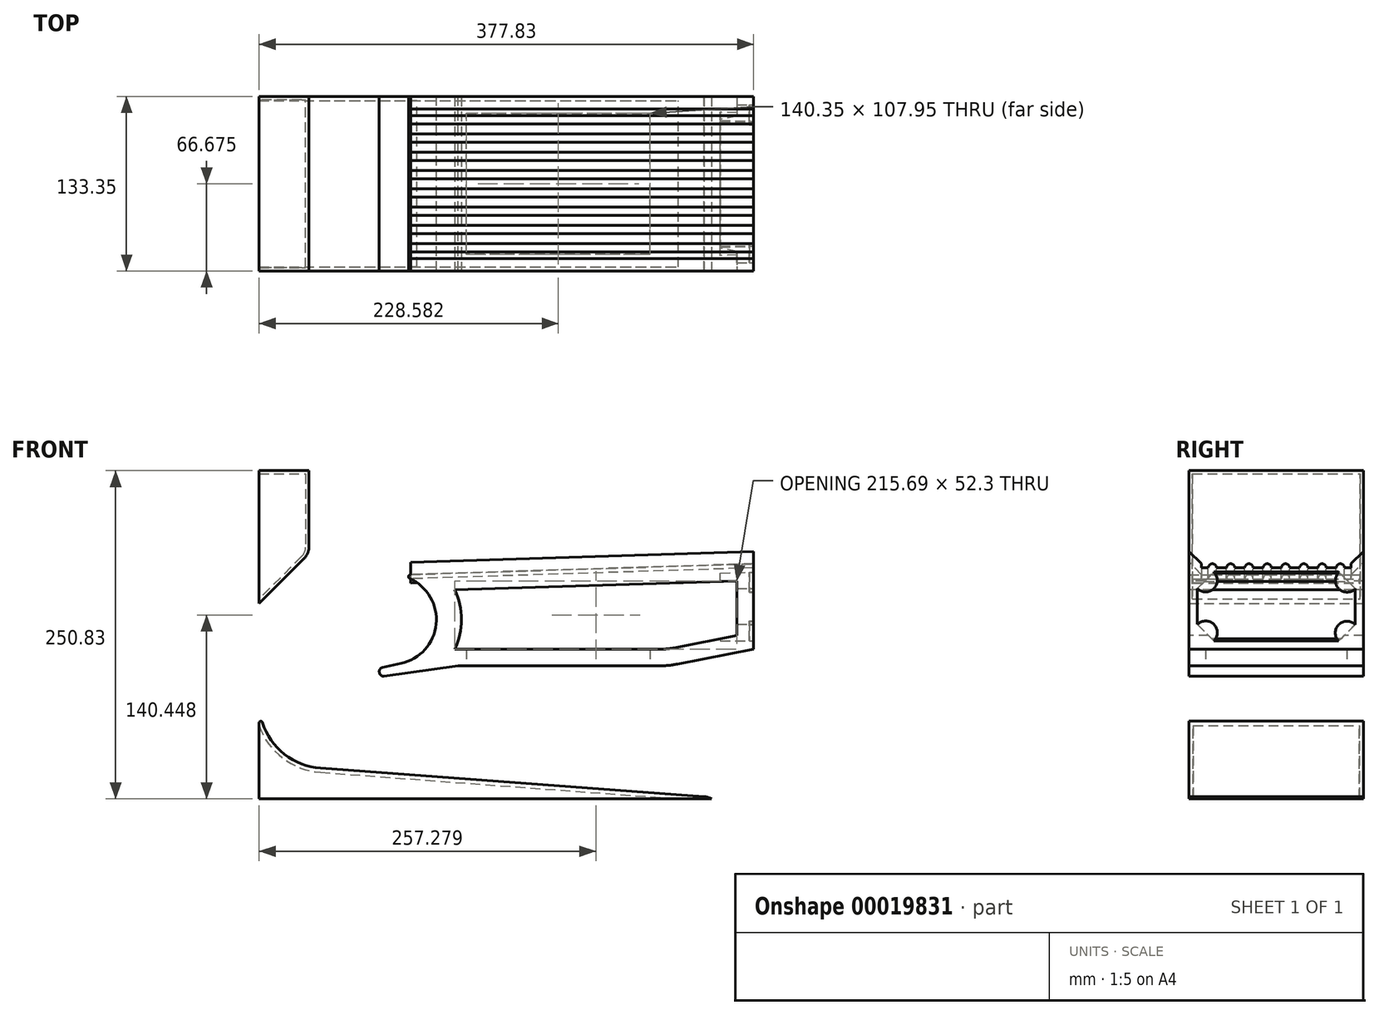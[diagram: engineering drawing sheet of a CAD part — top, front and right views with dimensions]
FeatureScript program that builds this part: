
annotation { "Feature Type Name" : "Feature", "Feature Type Description" : "" }
export const myFeature = defineFeature(function(context is Context, id is Id, definition is map)
    precondition{}
    {
        {
            var Q0;
            Q0=qCreatedBy(makeId("Front.planeOp"),FACE);
            var sketch = newSketch(context, id + "F0", { "sketchPlane" : qUnion([Q0])});
            skLineSegment(sketch, "E0.bottom", {"start": v(0, 0) * mm, "end": v(377.82, 0) * mm});
            skLineSegment(sketch, "E0.top", {"start": v(0, 250.83) * mm, "end": v(377.83, 250.83) * mm});
            skLineSegment(sketch, "E0.left", {"start": v(0, 74.15) * mm, "end": v(0, 250.82) * mm});
            skLineSegment(sketch, "E0.right", {"start": v(377.83, 0) * mm, "end": v(377.83, 250.83) * mm});
            skCircle(sketch, "E1", {"center": v(75.12, 58.13) * mm, "radius": 33.02 * mm});
            skArc(sketch, "E2", {"start": v(340.31, 1.68) * mm, "mid": v(359.23, 5.64) * mm, "end": v(373.15, 19.05) * mm});
            skLineSegment(sketch, "E3", {"start": v(377.83, 19.05) * mm, "end": v(373.15, 19.05) * mm});
            skLineSegment(sketch, "E4", {"start": v(47.03, 23.5) * mm, "end": v(340.31, 1.68) * mm});
            skPoint(sketch, "E5.visualSharp", {"position": v(0, 26.99) * mm});
            skArc(sketch, "E5.filletArc", {"start": v(2.48, 58.48) * mm, "mid": v(19.43, 34.2) * mm, "end": v(47.03, 23.5) * mm});
            skCircle(sketch, "E6.1.0.0", {"center": v(141.46, 52.73) * mm, "radius": 33.02 * mm});
            skCircle(sketch, "E6.2.0.0", {"center": v(207.8, 47.34) * mm, "radius": 33.02 * mm});
            skCircle(sketch, "E6.3.0.0", {"center": v(274.13, 41.94) * mm, "radius": 33.02 * mm});
            skCircle(sketch, "E6.4.0.0", {"center": v(340.47, 36.54) * mm, "radius": 33.02 * mm});
            skLineSegment(sketch, "E6.direction1", {"start": v(75.12, 58.13) * mm, "end": v(141.46, 52.73) * mm, "construction": true});
            skCircle(sketch, "E7", {"center": v(34.64, 111.21) * mm, "radius": 33.02 * mm});
            skLineSegment(sketch, "E8", {"start": v(377.83, 179.7) * mm, "end": v(115.72, 171.4) * mm});
            skArc(sketch, "E9.trimOffspring", {"start": v(108.42, 103.52) * mm, "mid": v(135.29, 133.5) * mm, "end": v(115.13, 168.36) * mm});
            skPoint(sketch, "E10.visualSharp", {"position": v(94.86, 170.74) * mm});
            skArc(sketch, "E10.filletArc", {"start": v(115.72, 171.4) * mm, "mid": v(114.21, 170.12) * mm, "end": v(115.13, 168.36) * mm});
            skCircle(sketch, "E11", {"center": v(96.26, 138.02) * mm, "radius": 33.02 * mm});
            skLineSegment(sketch, "E12", {"start": v(94.32, 100.47) * mm, "end": v(108.42, 103.52) * mm});
            skLineSegment(sketch, "E13", {"start": v(91.89, 96.7) * mm, "end": v(91.98, 96.26) * mm});
            skLineSegment(sketch, "E14", {"start": v(95.52, 93.78) * mm, "end": v(152.06, 101.6) * mm});
            skPoint(sketch, "E15.visualSharp", {"position": v(91.22, 99.8) * mm});
            skArc(sketch, "E15.filletArc", {"start": v(94.32, 100.47) * mm, "mid": v(92.32, 99.09) * mm, "end": v(91.89, 96.7) * mm});
            skPoint(sketch, "E16.visualSharp", {"position": v(92.6, 93.38) * mm});
            skArc(sketch, "E16.filletArc", {"start": v(91.98, 96.26) * mm, "mid": v(93.26, 94.32) * mm, "end": v(95.52, 93.78) * mm});
            skCircle(sketch, "E17.1.0.0", {"center": v(139.77, 207.48) * mm, "radius": 33.02 * mm});
            skCircle(sketch, "E17.2.0.0", {"center": v(206.9, 209.08) * mm, "radius": 33.02 * mm});
            skCircle(sketch, "E17.3.0.0", {"center": v(274.03, 210.68) * mm, "radius": 33.02 * mm});
            skCircle(sketch, "E17.4.0.0", {"center": v(341.17, 212.28) * mm, "radius": 33.02 * mm});
            skLineSegment(sketch, "E17.direction1", {"start": v(72.64, 205.88) * mm, "end": v(139.77, 207.48) * mm, "construction": true});
            skCircle(sketch, "E18.1.0.0", {"center": v(72.02, 201.09) * mm, "radius": 33.02 * mm});
            skLineSegment(sketch, "E19", {"start": v(38.1, 250.83) * mm, "end": v(38.1, 192.59) * mm});
            skLineSegment(sketch, "E20", {"start": v(34.38, 183.6) * mm, "end": v(0, 149.22) * mm});
            skPoint(sketch, "E21.visualSharp", {"position": v(38.1, 187.32) * mm});
            skArc(sketch, "E21.filletArc", {"start": v(34.38, 183.6) * mm, "mid": v(37.13, 187.73) * mm, "end": v(38.1, 192.59) * mm});
            skLineSegment(sketch, "E22", {"start": v(0, 0) * mm, "end": v(0, 58.09) * mm});
            skCircle(sketch, "E23", {"center": v(374.8, 54.39) * mm, "radius": 33.02 * mm});
            skLineSegment(sketch, "E24", {"start": v(305.1, 101.6) * mm, "end": v(152.06, 101.6) * mm});
            skPoint(sketch, "E25.orphan", {"position": v(312.44, 101.6) * mm});
            skLineSegment(sketch, "E26", {"start": v(319.64, 103) * mm, "end": v(377.83, 114.3) * mm});
            skPoint(sketch, "E27.orphan", {"position": v(377.83, 101.6) * mm});
            skArc(sketch, "E28.filletArc", {"start": v(305.1, 101.6) * mm, "mid": v(312.4, 101.95) * mm, "end": v(319.64, 103) * mm});
            skPoint(sketch, "E29.visualSharp", {"position": v(0, 74.15) * mm});
            skArc(sketch, "E29.filletArc", {"start": v(2.48, 58.48) * mm, "mid": v(1.07, 59.34) * mm, "end": v(0, 58.09) * mm});
            skSolve(sketch);
        }
        {
            var Q0;
            {var subQ2=sQuery(id+"F0.wireOp",EDGE,"E0.bottom");Q0=makeQuery(id+"F0.imprint","IMPRINT",FACE,{"disambiguationData":[TD([[makeQuery(id+"F0.imprint","IMPRINT",EDGE,{"derivedFrom":subQ2}),1.0]])]});}
            var Q1;
            {var subQ1=sQuery(id+"F0.wireOp",EDGE,"E8");Q1=makeQuery(id+"F0.imprint","IMPRINT",FACE,{"disambiguationData":[TD([[makeQuery(id+"F0.imprint","IMPRINT",EDGE,{"derivedFrom":subQ1}),1.0]])]});}
            var Q2;
            {var subQ1=sQuery(id+"F0.wireOp",EDGE,"E19");Q2=makeQuery(id+"F0.imprint","IMPRINT",FACE,{"disambiguationData":[TD([[makeQuery(id+"F0.imprint","IMPRINT",EDGE,{"derivedFrom":subQ1}),-1.0]])]});}
            extrude(context, id + "F1", {"entities" : qUnion([Q0, Q1, Q2]), "depth" : 133.35 * mm});
        }
        {
            var Q0;
            {var subQ0=sQuery(id+"F0.wireOp",EDGE,"E0.right");Q0=makeQuery(id+"F1.opExtrude","SWEPT_FACE",FACE,{"disambiguationData":[OSD([subQ0]),TDD([makeQuery(id+"F0.imprint","IMPRINT",EDGE,{"disambiguationData":[TD([[makeQuery(id+"F0.imprint","INTERSECT",VERTEX,{"derivedFrom":[subQ0,sQuery(id+"F0.wireOp",EDGE,"E8")]}),1.0]])],"derivedFrom":subQ0})])]});}
            var sketch = newSketch(context, id + "F2", { "sketchPlane" : qUnion([Q0])});
            skLineSegment(sketch, "E30.bottom", {"start": v(0, 179.7) * mm, "end": v(-98.4, 179.7) * mm});
            skLineSegment(sketch, "E30.top", {"start": v(0, 188.78) * mm, "end": v(-98.4, 188.78) * mm});
            skLineSegment(sketch, "E30.left", {"start": v(0, 179.7) * mm, "end": v(0, 188.78) * mm});
            skLineSegment(sketch, "E30.right", {"start": v(-98.4, 179.7) * mm, "end": v(-98.4, 188.78) * mm});
            skSolve(sketch);
        }
        {
            var Q0;
            Q0=makeQuery(id+"F1.opExtrude","CAP_FACE",FACE,{"disambiguationData":[OSD([sQuery(id+"F0.wireOp",EDGE,"E0.right"),sQuery(id+"F0.wireOp",EDGE,"E8"),sQuery(id+"F0.wireOp",EDGE,"E9.trimOffspring"),sQuery(id+"F0.wireOp",EDGE,"E10.filletArc"),sQuery(id+"F0.wireOp",EDGE,"E12"),sQuery(id+"F0.wireOp",EDGE,"E13"),sQuery(id+"F0.wireOp",EDGE,"E14"),sQuery(id+"F0.wireOp",EDGE,"E15.filletArc"),sQuery(id+"F0.wireOp",EDGE,"E16.filletArc"),sQuery(id+"F0.wireOp",EDGE,"E24"),sQuery(id+"F0.wireOp",EDGE,"E26"),sQuery(id+"F0.wireOp",EDGE,"E28.filletArc")])],"isStart":false});
            var sketch = newSketch(context, id + "F3", { "sketchPlane" : qUnion([Q0])});
            skLineSegment(sketch, "E31.0", {"start": v(365.13, 166.6) * mm, "end": v(149.44, 159.76) * mm});
            skLineSegment(sketch, "E32.0", {"start": v(305.1, 114.3) * mm, "end": v(149.43, 114.3) * mm});
            skArc(sketch, "E32.1", {"start": v(305.1, 114.3) * mm, "mid": v(311.19, 114.6) * mm, "end": v(317.21, 115.46) * mm});
            skLineSegment(sketch, "E32.2", {"start": v(317.21, 115.46) * mm, "end": v(365.13, 124.77) * mm});
            skLineSegment(sketch, "E32.3", {"start": v(365.13, 124.77) * mm, "end": v(365.13, 166.6) * mm});
            skArc(sketch, "E33.0", {"start": v(149.43, 114.3) * mm, "mid": v(154.52, 137.03) * mm, "end": v(149.44, 159.76) * mm});
            skSolve(sketch);
        }
        {
            var Q0;
            {var subQ6=sQuery(id+"F2.wireOp",EDGE,"E30.bottom");Q0=makeQuery(id+"F2.imprint","IMPRINT",FACE,{"disambiguationData":[TD([[makeQuery(id+"F2.imprint","IMPRINT",EDGE,{"derivedFrom":subQ6}),-1.0]])]});}
            var sketch = newSketch(context, id + "F4", { "sketchPlane" : qUnion([Q0])});
            skLineSegment(sketch, "E34.bottom", {"start": v(-114.3, 173.36) * mm, "end": v(-19.05, 173.36) * mm});
            skLineSegment(sketch, "E34.top", {"start": v(-114.3, 120.65) * mm, "end": v(-19.05, 120.65) * mm});
            skLineSegment(sketch, "E34.left", {"start": v(-127, 160.66) * mm, "end": v(-127, 133.35) * mm});
            skLineSegment(sketch, "E34.right", {"start": v(-6.35, 160.66) * mm, "end": v(-6.35, 133.35) * mm});
            skLineSegment(sketch, "E35", {"start": v(-127, 160.66) * mm, "end": v(-114.3, 173.36) * mm});
            skPoint(sketch, "E36.orphan", {"position": v(-127, 173.36) * mm});
            skLineSegment(sketch, "E37.MirrorCS", {"start": v(-6.35, 160.66) * mm, "end": v(-19.05, 173.36) * mm});
            skLineSegment(sketch, "E38.MirrorCS", {"start": v(-6.35, 133.35) * mm, "end": v(-19.05, 120.65) * mm});
            skPoint(sketch, "E39.start.orphan", {"position": v(-6.35, 147) * mm});
            skPoint(sketch, "E40.start.orphan", {"position": v(-66.68, 120.65) * mm});
            skPoint(sketch, "E41.orphan", {"position": v(-127, 120.65) * mm});
            skPoint(sketch, "E42.orphan", {"position": v(-6.35, 120.65) * mm});
            skPoint(sketch, "E43.orphan", {"position": v(-6.35, 173.36) * mm});
            skLineSegment(sketch, "E44.MirrorCS", {"start": v(-127, 133.35) * mm, "end": v(-114.3, 120.65) * mm});
            skPoint(sketch, "E45.end.orphan", {"position": v(-127, 147) * mm});
            skSolve(sketch);
        }
        {
            var Q0;
            Q0=makeQuery(id+"F1.opExtrude","CAP_FACE",FACE,{"disambiguationData":[OSD([sQuery(id+"F0.wireOp",EDGE,"E0.bottom"),sQuery(id+"F0.wireOp",EDGE,"E0.right"),sQuery(id+"F0.wireOp",EDGE,"E2"),sQuery(id+"F0.wireOp",EDGE,"E3"),sQuery(id+"F0.wireOp",EDGE,"E4"),sQuery(id+"F0.wireOp",EDGE,"E5.filletArc"),sQuery(id+"F0.wireOp",EDGE,"E22")])],"isStart":false});
            var sketch = newSketch(context, id + "F5", { "sketchPlane" : qUnion([Q0])});
            skLineSegment(sketch, "E46.bottom", {"start": v(377.83, 0) * mm, "end": v(345.84, 0) * mm});
            skLineSegment(sketch, "E46.top", {"start": v(377.83, 22.34) * mm, "end": v(345.84, 22.34) * mm});
            skLineSegment(sketch, "E46.left", {"start": v(377.83, 0) * mm, "end": v(377.83, 22.34) * mm});
            skLineSegment(sketch, "E46.right", {"start": v(345.84, 4.83) * mm, "end": v(345.84, 22.34) * mm});
            skLineSegment(sketch, "E47", {"start": v(345.84, 0) * mm, "end": v(345.64, 0.1) * mm});
            skLineSegment(sketch, "E48", {"start": v(340.31, 1.68) * mm, "end": v(339.94, 1.7) * mm});
            skPoint(sketch, "E49.visualSharp", {"position": v(342.98, 1.59) * mm});
            skArc(sketch, "E49.filletArc", {"start": v(345.64, 0.1) * mm, "mid": v(342.88, 1.24) * mm, "end": v(339.94, 1.7) * mm});
            skLineSegment(sketch, "E50", {"start": v(339.94, 1.7) * mm, "end": v(345.84, 4.83) * mm});
            skSolve(sketch);
        }
        {
            var Q0;
            Q0 = qSketchRegion(id + "F5", true);
            extrude(context, id + "F6", {"entities" : qUnion([Q0]), "operationType" : NewBodyOperationType.REMOVE, "endBound" : BoundingType.THROUGH_ALL, "oppositeDirection" : true, "depth" : 25.4 * mm});
        }
        {
            var Q0;
            Q0=makeQuery(id+"F1.opExtrude","SWEPT_FACE",FACE,{"disambiguationData":[OSD([sQuery(id+"F0.wireOp",EDGE,"E0.left")])]});
            shell(context, id + "F7", {"entities" : qUnion([Q0]), "thickness" : 2.54 * mm});
        }
        {
            var Q0;
            {var subQ6=sQuery(id+"F2.wireOp",EDGE,"E30.bottom");Q0=makeQuery(id+"F2.imprint","IMPRINT",FACE,{"disambiguationData":[TD([[makeQuery(id+"F2.imprint","IMPRINT",EDGE,{"derivedFrom":subQ6}),-1.0]])]});}
            var sketch = newSketch(context, id + "F8", { "sketchPlane" : qUnion([Q0])});
            skLineSegment(sketch, "E51", {"start": v(-123.83, 176.53) * mm, "end": v(-118.74, 176.53) * mm});
            skArc(sketch, "E52", {"start": v(-112.4, 176.53) * mm, "mid": v(-115.57, 179.7) * mm, "end": v(-118.75, 176.53) * mm});
            skArc(sketch, "E53.1.0.0", {"start": v(-98.43, 176.53) * mm, "mid": v(-101.6, 179.7) * mm, "end": v(-104.78, 176.53) * mm});
            skArc(sketch, "E53.2.0.0", {"start": v(-84.46, 176.53) * mm, "mid": v(-87.63, 179.7) * mm, "end": v(-90.8, 176.53) * mm});
            skArc(sketch, "E53.3.0.0", {"start": v(-70.49, 176.53) * mm, "mid": v(-73.66, 179.7) * mm, "end": v(-76.84, 176.53) * mm});
            skArc(sketch, "E53.4.0.0", {"start": v(-56.52, 176.53) * mm, "mid": v(-59.7, 179.7) * mm, "end": v(-62.87, 176.53) * mm});
            skArc(sketch, "E53.5.0.0", {"start": v(-42.55, 176.53) * mm, "mid": v(-45.72, 179.7) * mm, "end": v(-48.9, 176.53) * mm});
            skArc(sketch, "E53.6.0.0", {"start": v(-28.58, 176.53) * mm, "mid": v(-31.75, 179.7) * mm, "end": v(-34.93, 176.53) * mm});
            skArc(sketch, "E53.7.0.0", {"start": v(-14.6, 176.53) * mm, "mid": v(-17.78, 179.7) * mm, "end": v(-20.96, 176.53) * mm});
            skLineSegment(sketch, "E53.direction1", {"start": v(-112.4, 176.53) * mm, "end": v(-101.6, 176.53) * mm, "construction": true});
            skLineSegment(sketch, "E54.trimOffspring", {"start": v(-112.4, 176.53) * mm, "end": v(-104.78, 176.53) * mm});
            skLineSegment(sketch, "E55.trimOffspring", {"start": v(-70.49, 176.53) * mm, "end": v(-62.87, 176.53) * mm});
            skLineSegment(sketch, "E56.trimOffspring", {"start": v(-28.58, 176.53) * mm, "end": v(-20.96, 176.53) * mm});
            skLineSegment(sketch, "E57.trimOffspring", {"start": v(-14.6, 176.53) * mm, "end": v(-9.53, 176.53) * mm});
            skLineSegment(sketch, "E58", {"start": v(-42.55, 176.53) * mm, "end": v(-34.93, 176.53) * mm});
            skLineSegment(sketch, "E59", {"start": v(-56.52, 176.53) * mm, "end": v(-48.9, 176.53) * mm});
            skLineSegment(sketch, "E60", {"start": v(-84.46, 176.53) * mm, "end": v(-76.84, 176.53) * mm});
            skLineSegment(sketch, "E61", {"start": v(-98.43, 176.53) * mm, "end": v(-90.8, 176.53) * mm});
            skLineSegment(sketch, "E62", {"start": v(-123.83, 176.53) * mm, "end": v(-123.83, 179.7) * mm});
            skLineSegment(sketch, "E63", {"start": v(-115.57, 179.7) * mm, "end": v(-123.83, 179.7) * mm});
            skLineSegment(sketch, "E64", {"start": v(-115.57, 179.7) * mm, "end": v(-9.52, 179.7) * mm});
            skLineSegment(sketch, "E65", {"start": v(-9.53, 176.53) * mm, "end": v(-9.53, 179.7) * mm});
            skPoint(sketch, "E66.orphan", {"position": v(0, 176.53) * mm});
            skPoint(sketch, "E67.orphan", {"position": v(0, 179.7) * mm});
            skPoint(sketch, "E68.start.orphan", {"position": v(-133.35, 176.53) * mm});
            skSolve(sketch);
        }
        {
            var Q0;
            Q0 = qSketchRegion(id + "F8", true);
            var Q1;
            Q1=makeQuery(id+"F1.opExtrude","CAP_EDGE",EDGE,{"disambiguationData":[OSD([sQuery(id+"F0.wireOp",EDGE,"E8")])],"isStart":false});
            sweep(context, id + "F9", {"operationType" : NewBodyOperationType.REMOVE, "profiles" : qUnion([Q0]), "path" : qUnion([Q1])});
        }
        {
            var Q0;
            {var subQ6=sQuery(id+"F2.wireOp",EDGE,"E30.bottom");Q0=makeQuery(id+"F2.imprint","IMPRINT",FACE,{"disambiguationData":[TD([[makeQuery(id+"F2.imprint","IMPRINT",EDGE,{"derivedFrom":subQ6}),-1.0]])]});}
            var sketch = newSketch(context, id + "F10", { "sketchPlane" : qUnion([Q0])});
            skLineSegment(sketch, "E69", {"start": v(-133.35, 189.1) * mm, "end": v(-133.35, 179.58) * mm});
            skLineSegment(sketch, "E70", {"start": v(-133.35, 179.58) * mm, "end": v(-123.83, 179.58) * mm});
            skLineSegment(sketch, "E71", {"start": v(-123.83, 179.58) * mm, "end": v(-123.83, 179.7) * mm});
            skLineSegment(sketch, "E72", {"start": v(-123.83, 179.7) * mm, "end": v(-133.35, 189.1) * mm});
            skLineSegment(sketch, "E73.MirrorCS", {"start": v(-9.52, 179.7) * mm, "end": v(0, 189.1) * mm});
            skLineSegment(sketch, "E74.MirrorCS", {"start": v(-9.52, 179.58) * mm, "end": v(-9.52, 179.7) * mm});
            skLineSegment(sketch, "E75.MirrorCS", {"start": v(0, 179.58) * mm, "end": v(-9.53, 179.58) * mm});
            skLineSegment(sketch, "E76.MirrorCS", {"start": v(0, 189.1) * mm, "end": v(0, 179.58) * mm});
            skSolve(sketch);
        }
        {
            var Q0;
            Q0 = qSketchRegion(id + "F10", true);
            var Q1;
            Q1=makeQuery(id+"F1.opExtrude","CAP_EDGE",EDGE,{"disambiguationData":[OSD([sQuery(id+"F0.wireOp",EDGE,"E8")])],"isStart":false});
            sweep(context, id + "F11", {"operationType" : NewBodyOperationType.ADD, "profiles" : qUnion([Q0]), "path" : qUnion([Q1])});
        }
        {
            var Q0;
            Q0 = qSketchRegion(id + "F3", true);
            extrude(context, id + "F12", {"entities" : qUnion([Q0]), "operationType" : NewBodyOperationType.REMOVE, "endBound" : BoundingType.THROUGH_ALL, "oppositeDirection" : true, "depth" : 25.4 * mm});
        }
        {
            var Q0;
            Q0 = qSketchRegion(id + "F4", true);
            extrude(context, id + "F13", {"entities" : qUnion([Q0]), "operationType" : NewBodyOperationType.REMOVE, "oppositeDirection" : true, "depth" : 25.4 * mm});
        }
        {
            var Q0;
            Q0=qCreatedBy(makeId("Right.planeOp"),FACE);
            cPlane(context, id + "F14", {"entities" : qUnion([Q0]), "cplaneType" : CPlaneType.OFFSET, "offset" : 339.72 * mm, "width" : 152.4 * mm, "height" : 152.4 * mm});
        }
        {
            var Q0;
            Q0=makeQuery(id+"F1.opExtrude","SWEPT_FACE",FACE,{"disambiguationData":[OSD([sQuery(id+"F0.wireOp",EDGE,"E0.bottom")])]});
            var Q1;
            Q1=makeQuery(id+"F1.opExtrude","SWEPT_FACE",FACE,{"disambiguationData":[OSD([sQuery(id+"F0.wireOp",EDGE,"E22")])]});
            shell(context, id + "F15", {"entities" : qUnion([Q0, Q1]), "thickness" : 3.17 * mm});
        }
        {
            var Q0;
            {var subQ0=sQuery(id+"F0.wireOp",EDGE,"E8");Q0=makeQuery(id+"F11.boolean.opBoolean","MERGE",FACE,{"derivedFrom":[makeQuery(id+"F1.opExtrude","CAP_FACE",FACE,{"disambiguationData":[OSD([sQuery(id+"F0.wireOp",EDGE,"E0.right"),subQ0,sQuery(id+"F0.wireOp",EDGE,"E9.trimOffspring"),sQuery(id+"F0.wireOp",EDGE,"E10.filletArc"),sQuery(id+"F0.wireOp",EDGE,"E12"),sQuery(id+"F0.wireOp",EDGE,"E13"),sQuery(id+"F0.wireOp",EDGE,"E14"),sQuery(id+"F0.wireOp",EDGE,"E15.filletArc"),sQuery(id+"F0.wireOp",EDGE,"E16.filletArc"),sQuery(id+"F0.wireOp",EDGE,"E24"),sQuery(id+"F0.wireOp",EDGE,"E26"),sQuery(id+"F0.wireOp",EDGE,"E28.filletArc")])],"isStart":true}),makeQuery(id+"F11.opSweep","SWEPT_FACE",FACE,{"disambiguationData":[OSD([subQ0,sQuery(id+"F10.wireOp",EDGE,"E76.MirrorCS")])]})]});}
            cPlane(context, id + "F16", {"entities" : qUnion([Q0]), "cplaneType" : CPlaneType.OFFSET, "offset" : 66.67 * mm, "oppositeDirection" : true, "width" : 152.4 * mm, "height" : 152.4 * mm});
        }
        {
            var Q0;
            Q0=makeQuery(id+"F9.boolean.opBoolean","COPY",FACE,{"derivedFrom":makeQuery(id+"F9.opSweep","SWEPT_FACE",FACE,{"disambiguationData":[OSD([sQuery(id+"F0.wireOp",EDGE,"E8"),sQuery(id+"F8.wireOp",EDGE,"E60")])]})});
            var sketch = newSketch(context, id + "F17", { "sketchPlane" : qUnion([Q0])});
            skLineSegment(sketch, "E77.bottom", {"start": v(121, -130.18) * mm, "end": v(383.33, -130.17) * mm});
            skLineSegment(sketch, "E77.top", {"start": v(121, -3.18) * mm, "end": v(383.33, -3.17) * mm});
            skLineSegment(sketch, "E77.left", {"start": v(121, -130.18) * mm, "end": v(121, -3.18) * mm});
            skLineSegment(sketch, "E77.right", {"start": v(383.33, -130.17) * mm, "end": v(383.33, -3.17) * mm});
            skSolve(sketch);
        }
        {
            var Q0;
            Q0 = qSketchRegion(id + "F17", true);
            extrude(context, id + "F18", {"entities" : qUnion([Q0]), "operationType" : NewBodyOperationType.ADD, "oppositeDirection" : true, "depth" : 3.17 * mm});
        }
        {
            var Q0;
            {var subQ16=sQuery(id+"F8.wireOp",EDGE,"E51");Q0=makeQuery(id+"F8.imprint","IMPRINT",FACE,{"disambiguationData":[TD([[makeQuery(id+"F8.imprint","IMPRINT",EDGE,{"derivedFrom":subQ16}),-1.0]])]});}
            var sketch = newSketch(context, id + "F19", { "sketchPlane" : qUnion([Q0])});
            skLineSegment(sketch, "E78.bottom", {"start": v(-138.63, 187.5) * mm, "end": v(18.2, 187.5) * mm});
            skLineSegment(sketch, "E78.top", {"start": v(-138.63, 162.02) * mm, "end": v(18.2, 162.02) * mm});
            skLineSegment(sketch, "E78.left", {"start": v(-138.63, 187.5) * mm, "end": v(-138.63, 162.02) * mm});
            skLineSegment(sketch, "E78.right", {"start": v(18.2, 187.5) * mm, "end": v(18.2, 162.02) * mm});
            skSolve(sketch);
        }
        {
            var Q0;
            Q0 = qSketchRegion(id + "F19", true);
            extrude(context, id + "F20", {"entities" : qUnion([Q0]), "operationType" : NewBodyOperationType.REMOVE, "depth" : 25.4 * mm});
        }
        {
            var Q0;
            {var subQ16=sQuery(id+"F8.wireOp",EDGE,"E51");Q0=makeQuery(id+"F8.imprint","IMPRINT",FACE,{"disambiguationData":[TD([[makeQuery(id+"F8.imprint","IMPRINT",EDGE,{"derivedFrom":subQ16}),-1.0]])]});}
            var sketch = newSketch(context, id + "F21", { "sketchPlane" : qUnion([Q0])});
            skCircle(sketch, "E79", {"center": v(-120.76, 166.98) * mm, "radius": 8.9 * mm});
            skCircle(sketch, "E80", {"center": v(-12.75, 126.92) * mm, "radius": 8.9 * mm});
            skCircle(sketch, "E81", {"center": v(-12.67, 166.9) * mm, "radius": 8.9 * mm});
            skCircle(sketch, "E82", {"center": v(-120.72, 127.06) * mm, "radius": 8.9 * mm});
            skSolve(sketch);
        }
        {
            var Q0;
            Q0 = qSketchRegion(id + "F21", true);
            extrude(context, id + "F22", {"entities" : qUnion([Q0]), "operationType" : NewBodyOperationType.ADD, "oppositeDirection" : true, "depth" : 3.17 * mm});
        }
        {
            var Q0;
            Q0=makeQuery(id+"F1.opExtrude","SWEPT_FACE",FACE,{"disambiguationData":[OSD([sQuery(id+"F0.wireOp",EDGE,"E24")])]});
            var sketch = newSketch(context, id + "F23", { "sketchPlane" : qUnion([Q0])});
            skLineSegment(sketch, "E83.0", {"start": v(298.76, 120.65) * mm, "end": v(158.4, 120.65) * mm});
            skLineSegment(sketch, "E84.0", {"start": v(158.4, 12.7) * mm, "end": v(298.76, 12.7) * mm});
            skLineSegment(sketch, "E85.0", {"start": v(158.4, 120.65) * mm, "end": v(158.4, 12.7) * mm});
            skLineSegment(sketch, "E86.0", {"start": v(298.76, 120.65) * mm, "end": v(298.76, 12.7) * mm});
            skSolve(sketch);
        }
        {
            var Q0;
            Q0 = qSketchRegion(id + "F23", true);
            extrude(context, id + "F24", {"entities" : qUnion([Q0]), "operationType" : NewBodyOperationType.REMOVE, "oppositeDirection" : true, "depth" : 25.4 * mm});
        }
        {
            var Q0;
            Q0=qCreatedBy(id+"F16.planeOp",FACE);
            var sketch = newSketch(context, id + "F25", { "sketchPlane" : qUnion([Q0])});
            skLineSegment(sketch, "E87.bottom", {"start": v(-402.1, 228.81) * mm, "end": v(-71.6, 228.81) * mm});
            skLineSegment(sketch, "E87.top", {"start": v(-402.1, 62.7) * mm, "end": v(-71.6, 62.7) * mm});
            skLineSegment(sketch, "E87.left", {"start": v(-402.1, 228.81) * mm, "end": v(-402.1, 62.7) * mm});
            skLineSegment(sketch, "E87.right", {"start": v(-71.6, 228.81) * mm, "end": v(-71.6, 62.7) * mm});
            skSolve(sketch);
        }
        {
            var Q0;
            Q0 = qSketchRegion(id + "F3", true);
            extrude(context, id + "F26", {"entities" : qUnion([Q0]), "operationType" : NewBodyOperationType.REMOVE, "endBound" : BoundingType.THROUGH_ALL, "oppositeDirection" : true, "depth" : 25.4 * mm});
        }
    });
